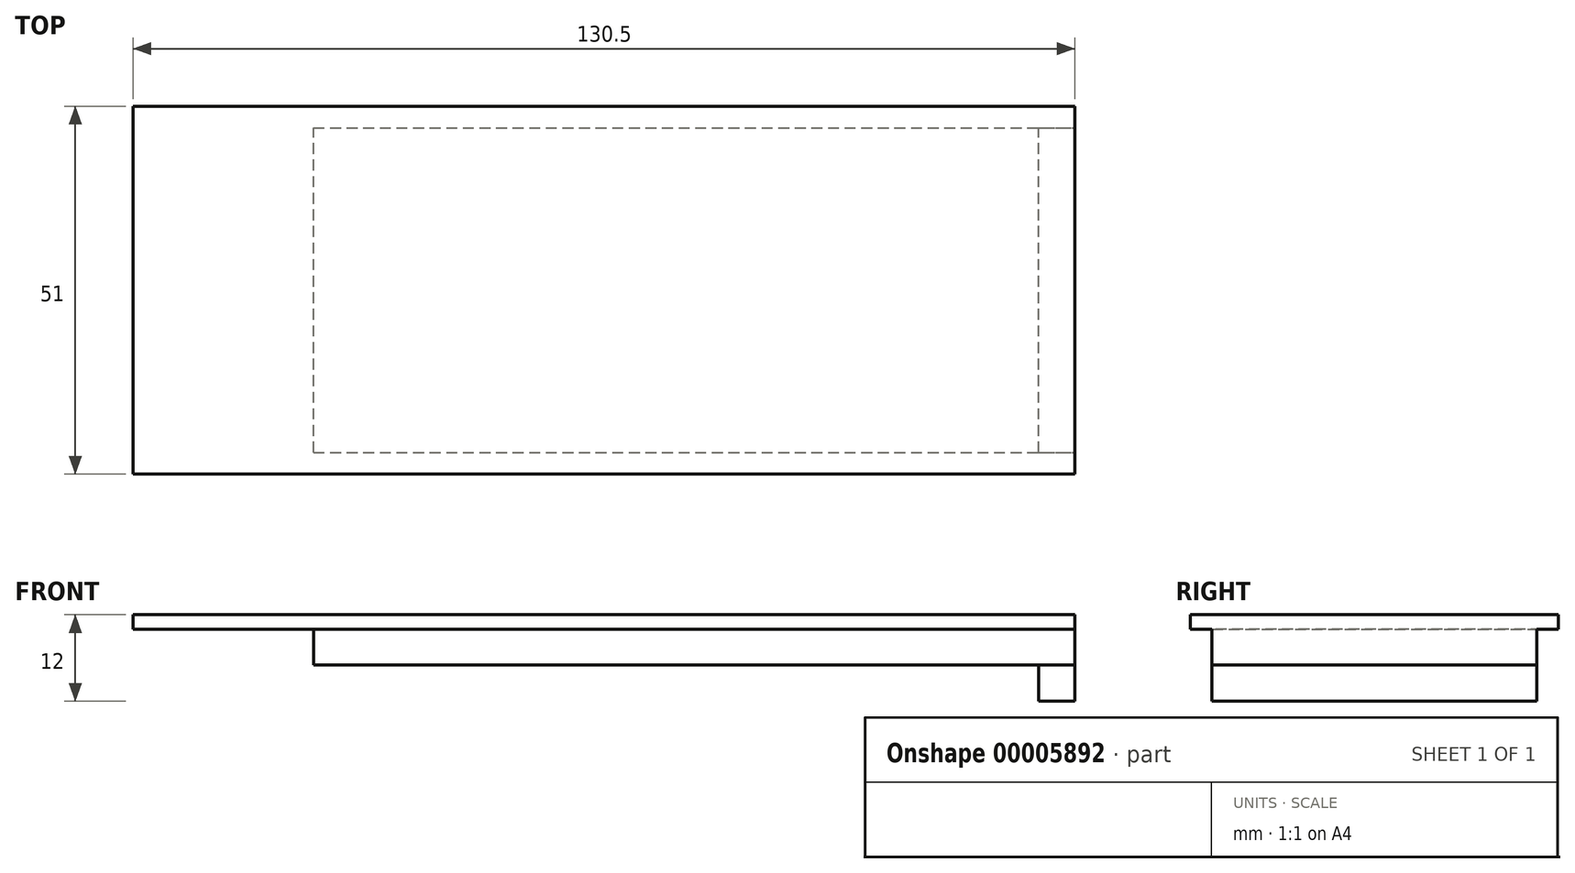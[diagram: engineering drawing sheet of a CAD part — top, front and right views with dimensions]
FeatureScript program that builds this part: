
annotation { "Feature Type Name" : "Feature", "Feature Type Description" : "" }
export const myFeature = defineFeature(function(context is Context, id is Id, definition is map)
    precondition{}
    {
        {
            var Q0;
            Q0=qCreatedBy(makeId("Top.planeOp"),FACE);
            var sketch = newSketch(context, id + "F0", { "sketchPlane" : qUnion([Q0])});
            skLineSegment(sketch, "E0.bottom", {"start": v(-10, 41) * mm, "end": v(120.5, 41) * mm});
            skLineSegment(sketch, "E0.top", {"start": v(-10, -10) * mm, "end": v(120.5, -10) * mm});
            skLineSegment(sketch, "E0.left", {"start": v(-10, 41) * mm, "end": v(-10, -10) * mm});
            skLineSegment(sketch, "E0.right", {"start": v(120.5, 41) * mm, "end": v(120.5, -10) * mm});
            skSolve(sketch);
        }
        {
            var Q0;
            Q0=makeQuery(id+"F0.imprint","IMPRINT",FACE,{"disambiguationData":[TD([[makeQuery(id+"F0.imprint","IMPRINT",EDGE,{"derivedFrom":sQuery(id+"F0.wireOp",EDGE,"E0.bottom")}),-1.0]])]});
            extrude(context, id + "F1", {"entities" : qUnion([Q0]), "depth" : 2 * mm});
        }
        {
            var Q0;
            Q0=makeQuery(id+"F1.opExtrude","CAP_FACE",FACE,{"disambiguationData":[OSD([sQuery(id+"F0.wireOp",EDGE,"E0.bottom"),sQuery(id+"F0.wireOp",EDGE,"E0.top"),sQuery(id+"F0.wireOp",EDGE,"E0.left"),sQuery(id+"F0.wireOp",EDGE,"E0.right")])],"isStart":true});
            var sketch = newSketch(context, id + "F2", { "sketchPlane" : qUnion([Q0])});
            skLineSegment(sketch, "E1.bottom", {"start": v(15, 7) * mm, "end": v(120.5, 7) * mm});
            skLineSegment(sketch, "E1.top", {"start": v(15, -38) * mm, "end": v(120.5, -38) * mm});
            skLineSegment(sketch, "E1.left", {"start": v(15, 7) * mm, "end": v(15, -38) * mm});
            skLineSegment(sketch, "E1.right", {"start": v(120.5, 7) * mm, "end": v(120.5, -38) * mm});
            skSolve(sketch);
        }
        {
            var Q0;
            Q0 = qSketchRegion(id + "F2", true);
            extrude(context, id + "F3", {"entities" : qUnion([Q0]), "operationType" : NewBodyOperationType.ADD, "depth" : 5 * mm});
        }
        {
            var Q0;
            Q0=makeQuery(id+"F3.opExtrude","CAP_FACE",FACE,{"disambiguationData":[OSD([sQuery(id+"F2.wireOp",EDGE,"E1.bottom"),sQuery(id+"F2.wireOp",EDGE,"E1.top"),sQuery(id+"F2.wireOp",EDGE,"E1.left"),sQuery(id+"F2.wireOp",EDGE,"E1.right")])],"isStart":false});
            var sketch = newSketch(context, id + "F4", { "sketchPlane" : qUnion([Q0])});
            skLineSegment(sketch, "E2.bottom", {"start": v(120.5, 7) * mm, "end": v(115.5, 7) * mm});
            skLineSegment(sketch, "E2.top", {"start": v(120.5, -38) * mm, "end": v(115.5, -38) * mm});
            skLineSegment(sketch, "E2.left", {"start": v(120.5, 7) * mm, "end": v(120.5, -38) * mm});
            skLineSegment(sketch, "E2.right", {"start": v(115.5, 7) * mm, "end": v(115.5, -38) * mm});
            skSolve(sketch);
        }
        {
            var Q0;
            Q0 = qSketchRegion(id + "F4", true);
            var Q1;
            Q1 = qBodyType(qCreatedBy(id + "F4" ,EDGE), BodyType.WIRE);
            var Q2;
            Q2=sQuery(id+"F4.wireOp",EDGE,"E2.left");
            extrude(context, id + "F5", {"entities" : qUnion([Q0]), "surfaceEntities" : qUnion([Q1, Q2]), "depth" : 5 * mm});
        }
    });
